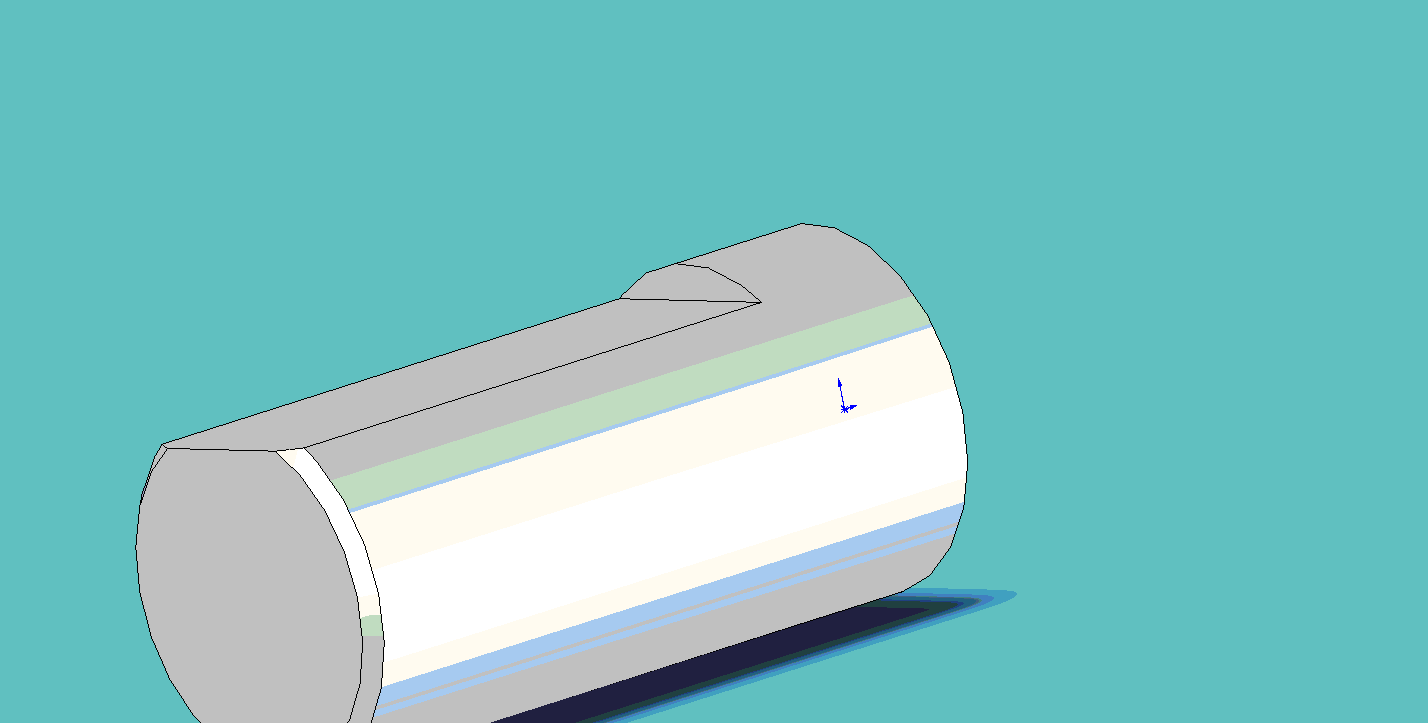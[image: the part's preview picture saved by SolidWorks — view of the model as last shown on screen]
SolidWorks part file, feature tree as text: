
SOLIDWORKS PART (.sldprt)
format: sldprt  version: not decoded by parser v0  size: 114,688 bytes
history: native  units: mm
features: plane x3, sketch x2, material x1, revolve x1, cut_extrude x1, chamfer x1 (+8 scaffold rows collapsed)
feature tree (17):
  scaffold x8  (default folders/planes/origin — collapsed)
  material  "Matériau <non spécifié>"
  plane  "Plan de face"
  plane  "Plan de dessus"
  plane  "Plan de droite"
  sketch  "Esquisse1"  dims[D1=5.0mm D2=10.15mm]
  revolve  "Révolution1"  Angle=360deg
  sketch  "Esquisse2"  dims[D1=4.5mm]
  cut_extrude  "Enlèv. mat.-Extru.1"  Depth=8mm
  chamfer  "Chanfrein1"  Distance=0.2mm Angle=45deg
decode coverage: 5 of 5 modeling features carry decoded parameters
note: suppression state not decoded; provenance and decode notes live in map.json
